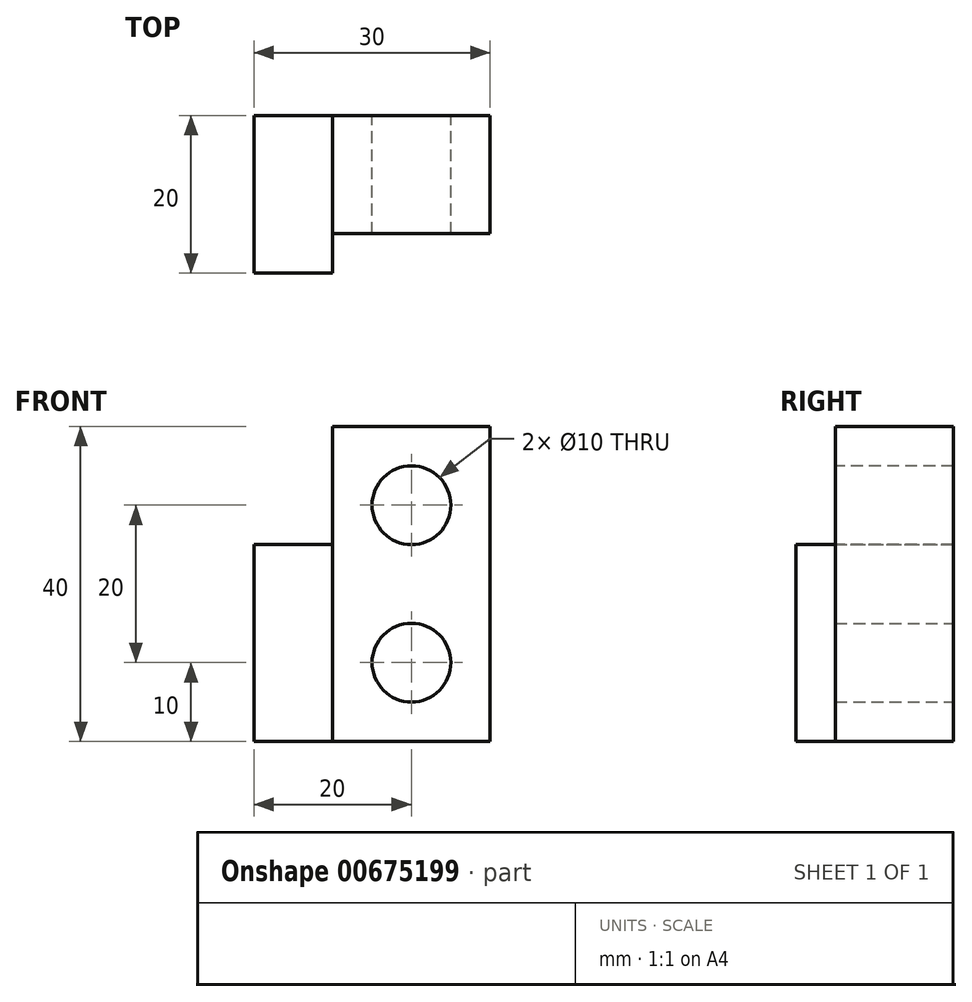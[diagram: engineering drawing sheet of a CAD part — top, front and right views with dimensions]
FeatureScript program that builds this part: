
annotation { "Feature Type Name" : "Feature", "Feature Type Description" : "" }
export const myFeature = defineFeature(function(context is Context, id is Id, definition is map)
    precondition{}
    {
        {
            var Q0;
            Q0=qCreatedBy(makeId("Front.planeOp"),FACE);
            var sketch = newSketch(context, id + "F0", { "sketchPlane" : qUnion([Q0])});
            skLineSegment(sketch, "E0.bottom", {"start": v(10, -20) * mm, "end": v(-10, -20) * mm});
            skLineSegment(sketch, "E0.top", {"start": v(10, 20) * mm, "end": v(-10, 20) * mm});
            skLineSegment(sketch, "E0.left", {"start": v(10, -20) * mm, "end": v(10, 20) * mm});
            skLineSegment(sketch, "E0.right", {"start": v(-10, -20) * mm, "end": v(-10, 20) * mm});
            skPoint(sketch, "E0.middle", {"position": v(0, 0) * mm});
            skLineSegment(sketch, "E1.bottom", {"start": v(-10, -20) * mm, "end": v(-20, -20) * mm});
            skLineSegment(sketch, "E1.top", {"start": v(-10, 5) * mm, "end": v(-20, 5) * mm});
            skLineSegment(sketch, "E1.left", {"start": v(-10, -20) * mm, "end": v(-10, 5) * mm});
            skLineSegment(sketch, "E1.right", {"start": v(-20, -20) * mm, "end": v(-20, 5) * mm});
            skCircle(sketch, "E2", {"center": v(0, -10) * mm, "radius": 5 * mm});
            skSolve(sketch);
        }
        {
            var Q0;
            Q0=makeQuery(id+"F0.imprint","IMPRINT",FACE,{"disambiguationData":[TD([[makeQuery(id+"F0.imprint","IMPRINT",EDGE,{"derivedFrom":sQuery(id+"F0.wireOp",EDGE,"E0.bottom")}),-1.0]])]});
            extrude(context, id + "F1", {"entities" : qUnion([Q0]), "depth" : 15 * mm, "offsetDistance" : 25 * mm});
        }
        {
            var Q0;
            Q0=makeQuery(id+"F0.imprint","IMPRINT",FACE,{"disambiguationData":[TD([[makeQuery(id+"F0.imprint","IMPRINT",EDGE,{"derivedFrom":sQuery(id+"F0.wireOp",EDGE,"E1.bottom")}),-1.0]])]});
            extrude(context, id + "F2", {"entities" : qUnion([Q0]), "operationType" : NewBodyOperationType.ADD, "depth" : 20 * mm, "offsetDistance" : 25 * mm});
        }
        {
            var Q0;
            Q0=makeQuery(id+"F1.opExtrude","CAP_FACE",FACE,{"disambiguationData":[OSD([sQuery(id+"F0.wireOp",EDGE,"E0.bottom"),sQuery(id+"F0.wireOp",EDGE,"E0.top"),sQuery(id+"F0.wireOp",EDGE,"E0.left"),sQuery(id+"F0.wireOp",EDGE,"E0.right"),sQuery(id+"F0.wireOp",EDGE,"E1.left"),sQuery(id+"F0.wireOp",EDGE,"E2")])],"isStart":false});
            var sketch = newSketch(context, id + "F3", { "sketchPlane" : qUnion([Q0])});
            skCircle(sketch, "E3", {"center": v(0, 10) * mm, "radius": 5 * mm});
            skSolve(sketch);
        }
        {
            var Q0;
            Q0 = qSketchRegion(id + "F3", true);
            var Q1;
            {var subQ0=sQuery(id+"F0.wireOp",EDGE,"E1.left");Q1=makeQuery(id+"F2.boolean.opBoolean","MERGE",FACE,{"derivedFrom":[makeQuery(id+"F1.opExtrude","CAP_FACE",FACE,{"disambiguationData":[OSD([sQuery(id+"F0.wireOp",EDGE,"E0.bottom"),sQuery(id+"F0.wireOp",EDGE,"E0.top"),sQuery(id+"F0.wireOp",EDGE,"E0.left"),sQuery(id+"F0.wireOp",EDGE,"E0.right"),subQ0,sQuery(id+"F0.wireOp",EDGE,"E2")])],"isStart":true}),makeQuery(id+"F2.opExtrude","CAP_FACE",FACE,{"disambiguationData":[OSD([sQuery(id+"F0.wireOp",EDGE,"E1.bottom"),sQuery(id+"F0.wireOp",EDGE,"E1.top"),subQ0,sQuery(id+"F0.wireOp",EDGE,"E1.right")])],"isStart":true})]});}
            extrude(context, id + "F4", {"entities" : qUnion([Q0]), "operationType" : NewBodyOperationType.REMOVE, "endBound" : BoundingType.UP_TO_SURFACE, "oppositeDirection" : true, "depth" : 25 * mm, "endBoundEntityFace" : qUnion([Q1]), "offsetDistance" : 25 * mm});
        }
    });
